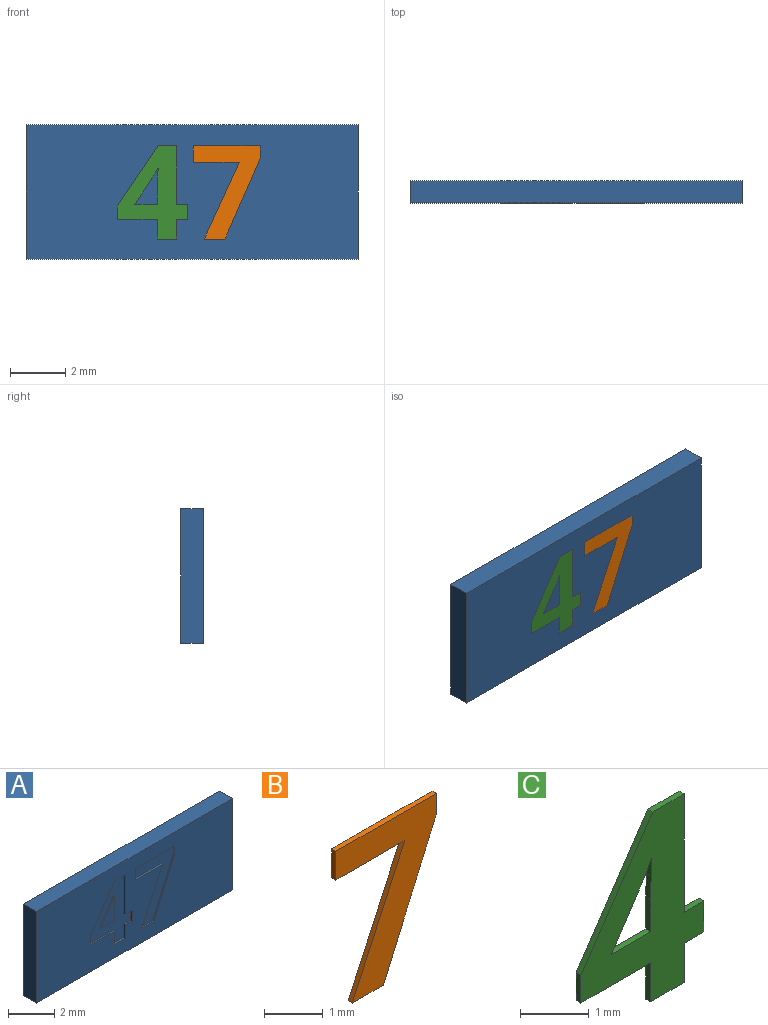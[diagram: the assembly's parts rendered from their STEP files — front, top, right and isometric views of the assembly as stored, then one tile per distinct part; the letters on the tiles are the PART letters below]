
ASSEMBLY  parts=3 mates=2
PART A: 34 faces, bbox 12x0.8x4.9 mm
  f0: plane 12x4.85mm, normal (0,-1,0), area 50mm2, adj f1,f2,f3,f4,f6,f7,f8,f9
  f1: plane 12x0.8mm, normal (0,0,-1), area 9.6mm2, adj f0,f2,f4,f5
  f2: plane 4.85x0.8mm, normal (1,0,0), area 3.9mm2, adj f0,f1,f3,f5
  f3: plane 12x0.8mm, normal (0,0,1), area 9.6mm2, adj f0,f2,f4,f5
  f4: plane 4.85x0.8mm, normal (-1,0,0), area 3.9mm2, adj f0,f1,f3,f5
  f5: plane 12x4.85mm, normal (0,1,0), area 58.2mm2, adj f1,f2,f3,f4
  f6: plane 0.55x0.1mm, normal (-1,0,0), area 0.1mm2, adj f0,f7,f23,f24
  f7: plane 0.41x0.1mm, normal (0,0,-1), area 0mm2, adj f0,f6,f8,f24
  f8: plane 2.12x0.1mm, normal (-1,0,0), area 0.2mm2, adj f0,f7,f9,f24
  f9: plane 0.66x0.1mm, normal (0,0,-1), area 0.1mm2, adj f0,f8,f10,f24
  f10: plane 2.18x1.48mm, normal (0.83,0,-0.56), area 0.3mm2, adj f0,f9,f11,f24
  f11: plane 0.5x0.1mm, normal (1,0,0), area 0mm2, adj f0,f10,f12,f24
  f12: plane 1.44x0.1mm, normal (0,0,1), area 0.1mm2, adj f0,f11,f13,f24
  f13: plane 0.7x0.1mm, normal (1,0,0), area 0.1mm2, adj f0,f12,f14,f24
  f14: plane 0.7x0.1mm, normal (0,0,1), area 0.1mm2, adj f0,f13,f15,f24
  f15: plane 0.7x0.1mm, normal (-1,0,0), area 0.1mm2, adj f0,f14,f23,f24
  f16: plane 0.81x0.1mm, normal (0,0,-1), area 0.1mm2, adj f17,f22,f24,f25
  f17: plane 0.93x0.62mm, normal (-0.83,0,0.55), area 0.1mm2, adj f16,f18,f24,f25
  f18: extruded ~0.37x0.21mm, area 0mm2, adj f17,f19,f24,f25
  f19: plane 0.1x0.02mm, normal (0,0,1), area 0mm2, adj f18,f20,f24,f25
  f20: extruded ~0.32x0.1mm, area 0mm2, adj f19,f21,f24,f25
  f21: extruded ~0.42x0.1mm, area 0mm2, adj f20,f22,f24,f25
  f22: plane 0.57x0.1mm, normal (1,0,0), area 0.1mm2, adj f16,f21,f24,f25
  f23: plane 0.41x0.1mm, normal (0,0,1), area 0mm2, adj f0,f6,f15,f24
  f24: plane 3.37x2.54mm, normal (0,-1,0), area 4.3mm2, adj f6,f7,f8,f9,f10,f11,f12,f13
  f25: plane 1.3x0.84mm, normal (0,-1,0), area 0.5mm2, adj f16,f17,f18,f19,f20,f21,f22
  f26: plane 0.75x0.1mm, normal (0,0,1), area 0.1mm2, adj f0,f27,f32,f33
  f27: plane 2.92x1.28mm, normal (-0.92,0,0.4), area 0.3mm2, adj f0,f26,f28,f33
  f28: plane 0.45x0.1mm, normal (-1,0,0), area 0mm2, adj f0,f27,f29,f33
  f29: plane 2.42x0.1mm, normal (0,0,-1), area 0.2mm2, adj f0,f28,f30,f33
  f30: plane 0.6x0.1mm, normal (1,0,0), area 0.1mm2, adj f0,f29,f31,f33
  f31: plane 1.66x0.1mm, normal (0,0,1), area 0.2mm2, adj f0,f30,f32,f33
  f32: plane 2.77x1.27mm, normal (0.91,0,-0.42), area 0.3mm2, adj f0,f26,f31,f33
  f33: plane 3.37x2.42mm, normal (0,-1,0), area 3.4mm2, adj f26,f27,f28,f29,f30,f31,f32
PART B: 9 faces, bbox 2.4x0.1x3.4 mm
  f0: plane 3.37x2.42mm, normal (0,-1,0), area 3.4mm2, adj f1,f2,f3,f4,f6,f7,f8
  f1: plane 2.92x1.28mm, normal (0.92,0,-0.4), area 0.3mm2, adj f0,f2,f5,f7
  f2: plane 0.45x0.1mm, normal (1,0,0), area 0mm2, adj f0,f1,f3,f5
  f3: plane 2.42x0.1mm, normal (0,0,1), area 0.2mm2, adj f0,f2,f4,f5
  f4: plane 0.6x0.1mm, normal (-1,0,0), area 0.1mm2, adj f0,f3,f5,f6
  f5: plane 3.37x2.42mm, normal (0,1,0), area 3.4mm2, adj f1,f2,f3,f4,f6,f7,f8
  f6: plane 1.66x0.1mm, normal (0,0,-1), area 0.2mm2, adj f0,f4,f5,f8
  f7: plane 0.75x0.1mm, normal (0,0,-1), area 0.1mm2, adj f0,f1,f5,f8
  f8: plane 2.77x1.27mm, normal (-0.91,0,0.42), area 0.3mm2, adj f0,f5,f6,f7
PART C: 20 faces, bbox 2.5x0.1x3.4 mm
  f0: plane 3.37x2.54mm, normal (0,-1,0), area 4.3mm2, adj f1,f2,f3,f4,f5,f6,f7,f8
  f1: plane 0.41x0.1mm, normal (0,0,1), area 0mm2, adj f0,f2,f13,f15
  f2: plane 2.12x0.1mm, normal (1,0,0), area 0.2mm2, adj f0,f1,f3,f13
  f3: plane 0.66x0.1mm, normal (0,0,1), area 0.1mm2, adj f0,f2,f4,f13
  f4: plane 2.18x1.48mm, normal (-0.83,0,0.56), area 0.3mm2, adj f0,f3,f5,f13
  f5: plane 0.5x0.1mm, normal (-1,0,0), area 0mm2, adj f0,f4,f6,f13
  f6: plane 1.44x0.1mm, normal (0,0,-1), area 0.1mm2, adj f0,f5,f7,f13
  f7: plane 0.7x0.1mm, normal (-1,0,0), area 0.1mm2, adj f0,f6,f8,f13
  f8: plane 0.7x0.1mm, normal (0,0,-1), area 0.1mm2, adj f0,f7,f13,f14
  f9: plane 0.93x0.62mm, normal (0.83,0,-0.55), area 0.1mm2, adj f0,f10,f13,f18
  f10: extruded ~0.37x0.21mm, area 0mm2, adj f0,f9,f11,f13
  f11: plane 0.1x0.02mm, normal (0,0,-1), area 0mm2, adj f0,f10,f12,f13
  f12: extruded ~0.32x0.1mm, area 0mm2, adj f0,f11,f13,f17
  f13: plane 3.37x2.54mm, normal (0,1,0), area 4.3mm2, adj f1,f2,f3,f4,f5,f6,f7,f8
  f14: plane 0.7x0.1mm, normal (1,0,0), area 0.1mm2, adj f0,f8,f13,f16
  f15: plane 0.55x0.1mm, normal (1,0,0), area 0.1mm2, adj f0,f1,f13,f16
  f16: plane 0.41x0.1mm, normal (0,0,-1), area 0mm2, adj f0,f13,f14,f15
  f17: extruded ~0.42x0.1mm, area 0mm2, adj f0,f12,f13,f19
  f18: plane 0.81x0.1mm, normal (0,0,1), area 0.1mm2, adj f0,f9,f13,f19
  f19: plane 0.57x0.1mm, normal (-1,0,0), area 0.1mm2, adj f0,f13,f17,f18
PLACE A t=(-0.01,0.4,0)mm
PLACE B t=(-0.23,0.4,0)mm
PLACE C t=(-2.89,0.4,0)mm
MATE fastened C.f0 <-> A.f0  axis (0,-1,0) through (-1.26,-0.4,-1.7)mm
MATE fastened B.f0 <-> A.f0  axis (0,-1,0) through (0.44,-0.4,-1.7)mm
